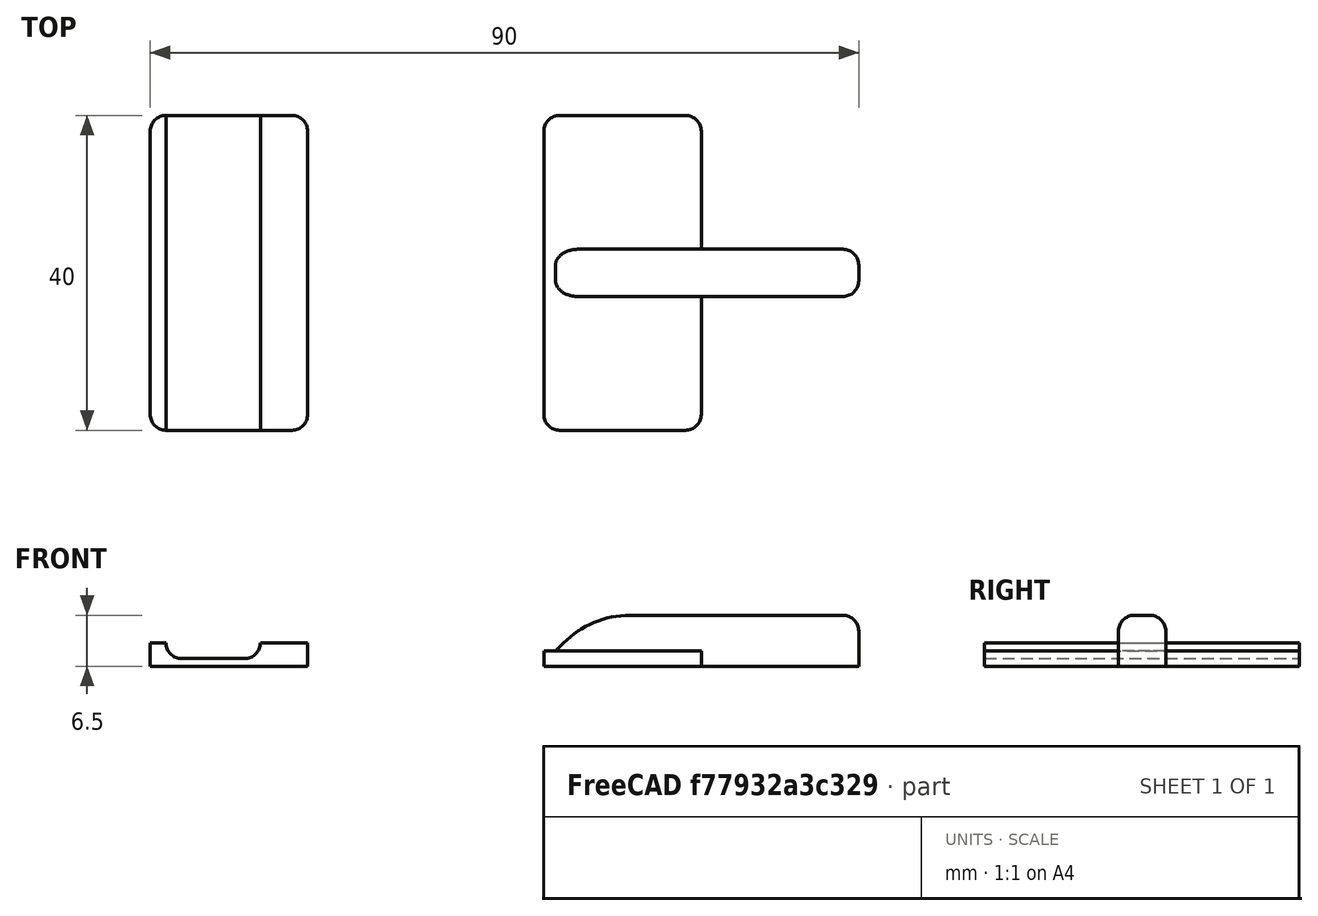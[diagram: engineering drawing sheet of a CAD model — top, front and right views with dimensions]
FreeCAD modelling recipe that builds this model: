
FCSTD DOCUMENT  (FreeCAD 0.19R)
Label: PhoneHolder
License: All rights reserved
LicenseURL: https://en.wikipedia.org/wiki/All_rights_reserved
objects: Part::Fillet×6, Part::Box×4, Part::Chamfer×1, Part::MultiFuse×1, Part::Cut×1
note: 13 computed .brp shape members not serialized (recipe doc carries the construction recipe); baked Part::Feature solids carry a one-line shape summary decoded from their .brp

FEATURE [Part::Box] Box  label="Cube"
  AttacherType = Attacher::AttachEngine3D
  Height = 2
  Length = 20
  Placement = pos=(-10,-20,0) rot=(0,0,1;0rad)
  Width = 40
FEATURE [Part::Fillet] Fillet  label="Base"
  Base = -> Box
  Edges = 4 edges r=2: [Edge1,Edge3,Edge5,Edge7]
FEATURE [Part::Box] Box001  label="Cube001"
  AttacherType = Attacher::AttachEngine3D
  Height = 6.5
  Length = 40
  Placement = pos=(-10,-3,0) rot=(0,0,1;0rad)
  Width = 6
FEATURE [Part::Chamfer] Chamfer
  Base = -> Box001
  Edges = 1 edges r=6: [Edge2]
FEATURE [Part::Fillet] Fillet001
  Base = -> Chamfer
  Edges = 1 edges r=12: [Edge10]
FEATURE [Part::Fillet] Fillet002
  Base = -> Fillet001
  Edges = 2 edges r=2: [Edge2,Edge12]
FEATURE [Part::Fillet] Fillet003  label="Limitter"
  Base = -> Fillet002
  Edges = 1 edges r=2: [Edge1]
FEATURE [Part::MultiFuse] Fusion  label="Top"
  Placement = pos=(50,0,0) rot=(0,0,1;0rad)
  Shapes = -> [Fillet003,Fillet]
FEATURE [Part::Box] Box002  label="Cube002"
  AttacherType = Attacher::AttachEngine3D
  Height = 3
  Length = 20
  Placement = pos=(-10,-20,0) rot=(0,0,1;0rad)
  Width = 40
FEATURE [Part::Fillet] Fillet004  label="Base001"
  Base = -> Box002
  Edges = 4 edges r=2: [Edge1,Edge3,Edge5,Edge7]
FEATURE [Part::Box] Box003  label="Cube003"
  AttacherType = Attacher::AttachEngine3D
  Height = 3
  Length = 12
  Placement = pos=(-8,-20,1) rot=(0,0,1;0rad)
  Width = 40
FEATURE [Part::Fillet] Fillet005
  Base = -> Box003
  Edges = 2 edges r=2: [Edge4,Edge8]
FEATURE [Part::Cut] Cut  label="Bottom"
  Base = -> Fillet004
  Tool = -> Fillet005
